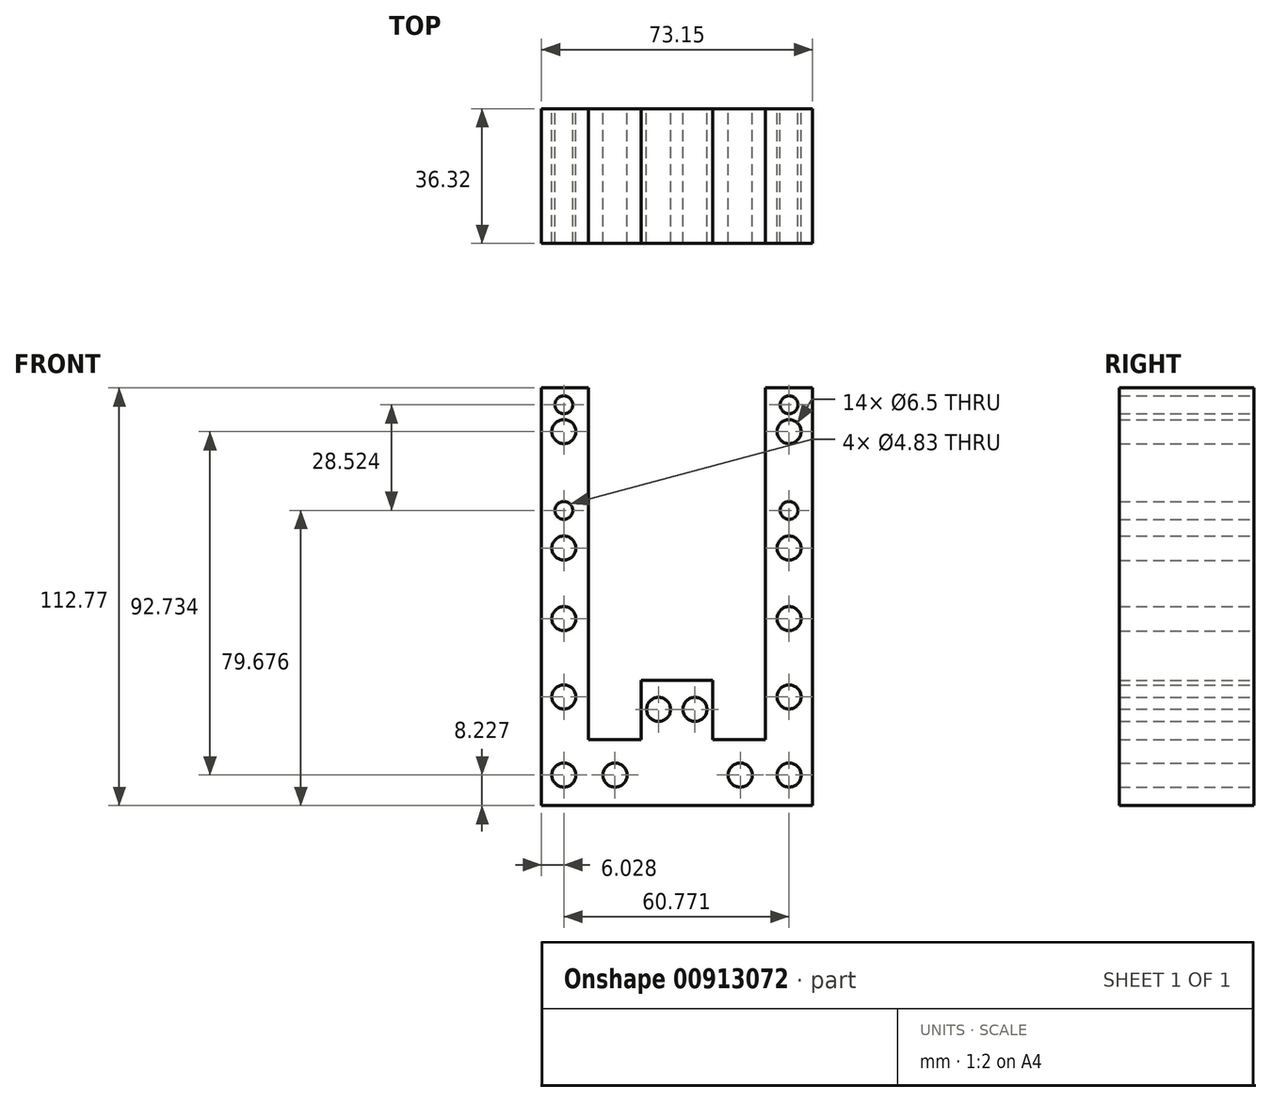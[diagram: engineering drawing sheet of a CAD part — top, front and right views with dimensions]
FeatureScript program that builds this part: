
annotation { "Feature Type Name" : "Feature", "Feature Type Description" : "" }
export const myFeature = defineFeature(function(context is Context, id is Id, definition is map)
    precondition{}
    {
        {
            var Q0;
            Q0=qCreatedBy(makeId("Front.planeOp"),FACE);
            var sketch = newSketch(context, id + "F0", { "sketchPlane" : qUnion([Q0])});
            skLineSegment(sketch, "E0", {"start": v(-36.05, 56.48) * mm, "end": v(-36.05, -56.3) * mm});
            skLineSegment(sketch, "E1", {"start": v(-36.05, -56.3) * mm, "end": v(37.1, -56.3) * mm});
            skLineSegment(sketch, "E2", {"start": v(37.1, -56.3) * mm, "end": v(37.1, 56.48) * mm});
            skLineSegment(sketch, "E3", {"start": v(37.1, 56.48) * mm, "end": v(24.4, 56.48) * mm});
            skLineSegment(sketch, "E4", {"start": v(-36.05, 56.48) * mm, "end": v(-23.35, 56.48) * mm});
            skLineSegment(sketch, "E5", {"start": v(24.4, 56.48) * mm, "end": v(24.4, -38.51) * mm});
            skLineSegment(sketch, "E6", {"start": v(-23.35, 56.48) * mm, "end": v(-23.35, -38.51) * mm});
            skLineSegment(sketch, "E7", {"start": v(-23.35, -38.51) * mm, "end": v(-9.13, -38.51) * mm});
            skLineSegment(sketch, "E8", {"start": v(24.4, -38.51) * mm, "end": v(10.17, -38.51) * mm});
            skLineSegment(sketch, "E9", {"start": v(10.17, -38.51) * mm, "end": v(10.17, -22.51) * mm});
            skLineSegment(sketch, "E10", {"start": v(-9.13, -38.51) * mm, "end": v(-9.13, -22.51) * mm});
            skLineSegment(sketch, "E11", {"start": v(-9.13, -22.51) * mm, "end": v(10.17, -22.51) * mm});
            skCircle(sketch, "E12", {"center": v(30.75, 51.91) * mm, "radius": 2.41 * mm});
            skCircle(sketch, "E13", {"center": v(-30.02, 51.91) * mm, "radius": 2.41 * mm});
            skCircle(sketch, "E14", {"center": v(30.75, 23.39) * mm, "radius": 2.41 * mm});
            skCircle(sketch, "E15", {"center": v(-30.02, 23.39) * mm, "radius": 2.41 * mm});
            skCircle(sketch, "E16", {"center": v(-30.02, 44.67) * mm, "radius": 3.25 * mm});
            skCircle(sketch, "E17", {"center": v(30.75, 44.67) * mm, "radius": 3.25 * mm});
            skCircle(sketch, "E18", {"center": v(-30.02, 13.2) * mm, "radius": 3.25 * mm});
            skCircle(sketch, "E19", {"center": v(30.75, 13.2) * mm, "radius": 3.25 * mm});
            skCircle(sketch, "E20", {"center": v(-30.02, -5.84) * mm, "radius": 3.25 * mm});
            skCircle(sketch, "E21", {"center": v(30.75, -5.84) * mm, "radius": 3.25 * mm});
            skCircle(sketch, "E22", {"center": v(-30.02, -26.95) * mm, "radius": 3.25 * mm});
            skCircle(sketch, "E23", {"center": v(30.75, -26.95) * mm, "radius": 3.25 * mm});
            skCircle(sketch, "E24", {"center": v(-30.02, -48.06) * mm, "radius": 3.25 * mm});
            skCircle(sketch, "E25", {"center": v(30.75, -48.06) * mm, "radius": 3.25 * mm});
            skCircle(sketch, "E26", {"center": v(-16.22, -48.06) * mm, "radius": 3.25 * mm});
            skCircle(sketch, "E27", {"center": v(17.56, -48.06) * mm, "radius": 3.25 * mm});
            skCircle(sketch, "E28", {"center": v(-4.47, -30.33) * mm, "radius": 3.25 * mm});
            skCircle(sketch, "E29", {"center": v(5.35, -30.33) * mm, "radius": 3.25 * mm});
            skSolve(sketch);
        }
        {
            var Q0;
            Q0 = qSketchRegion(id + "F0", true);
            extrude(context, id + "F1", {"entities" : qUnion([Q0]), "endBound" : BoundingType.SYMMETRIC, "depth" : 36.32 * mm, "offsetDistance" : 25.4 * mm});
        }
    });
